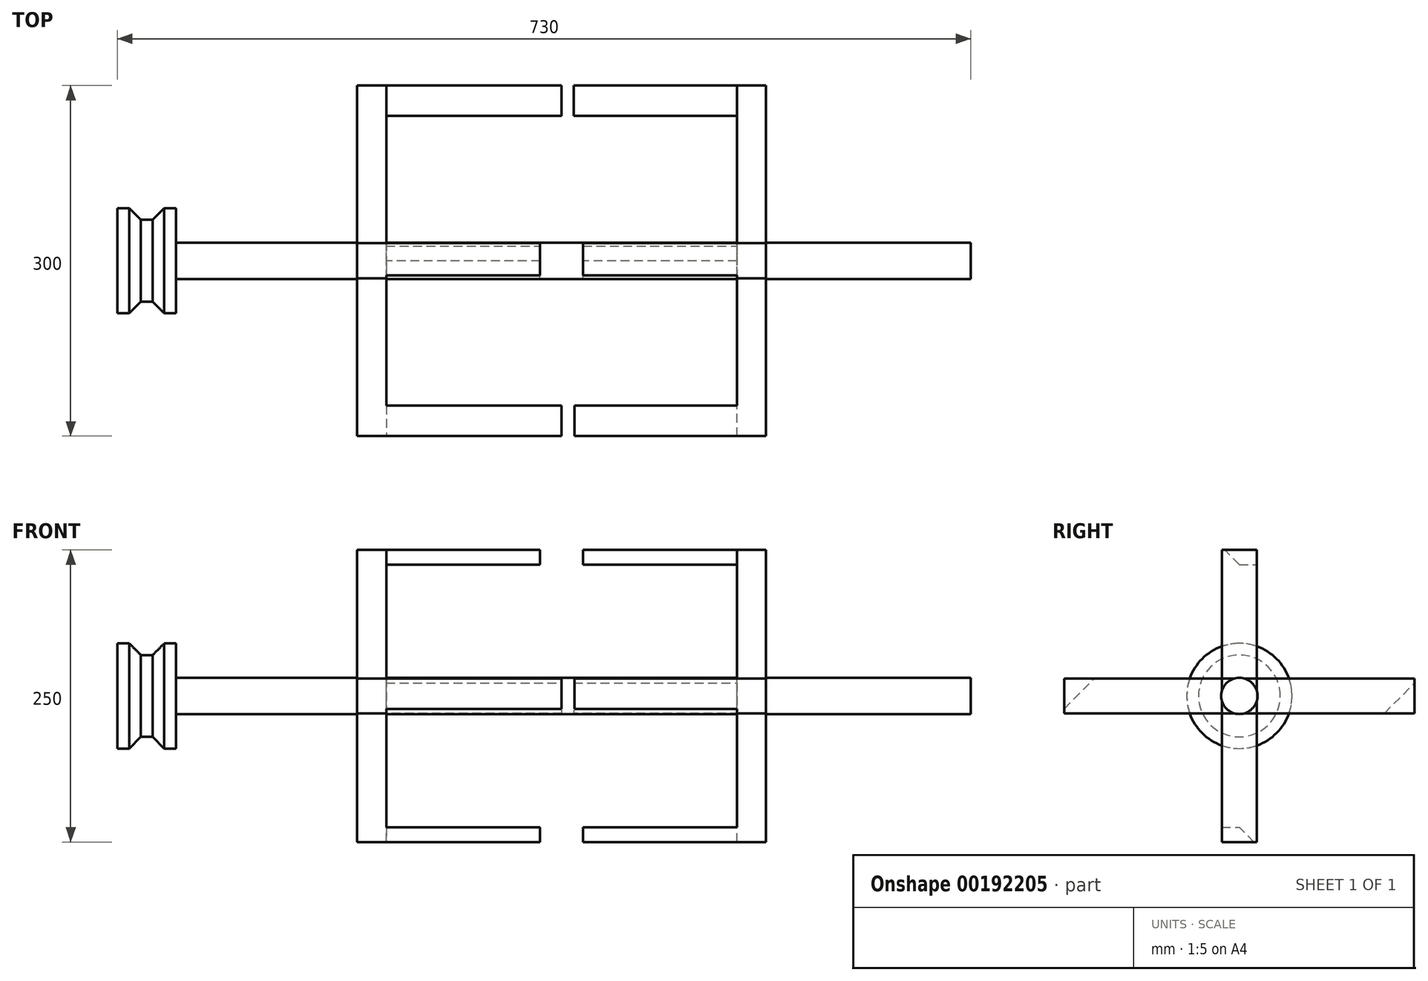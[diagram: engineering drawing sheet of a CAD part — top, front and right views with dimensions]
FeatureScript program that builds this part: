
annotation { "Feature Type Name" : "Feature", "Feature Type Description" : "" }
export const myFeature = defineFeature(function(context is Context, id is Id, definition is map)
    precondition{}
    {
        {
            var Q0;
            Q0=qCreatedBy(makeId("Front.planeOp"),FACE);
            var sketch = newSketch(context, id + "F0", { "sketchPlane" : qUnion([Q0])});
            skPoint(sketch, "E0.middle", {"position": v(0, 0) * mm});
            skLineSegment(sketch, "E1.trimOffspring", {"start": v(-83.52, 150) * mm, "end": v(-200, 150) * mm});
            skLineSegment(sketch, "E2.bottom", {"start": v(-350, 15.5) * mm, "end": v(350, 15.5) * mm});
            skLineSegment(sketch, "E2.top", {"start": v(-350, -15.5) * mm, "end": v(350, -15.5) * mm});
            skLineSegment(sketch, "E2.left", {"start": v(-350, 15.5) * mm, "end": v(-350, -15.5) * mm});
            skLineSegment(sketch, "E2.right", {"start": v(350, 15.5) * mm, "end": v(350, -15.5) * mm});
            skLineSegment(sketch, "E3", {"start": v(350, 0) * mm, "end": v(-350, 0) * mm});
            skLineSegment(sketch, "E4.bottom", {"start": v(-175, -125) * mm, "end": v(-18.4, -125) * mm});
            skLineSegment(sketch, "E4.top", {"start": v(-175, 125) * mm, "end": v(-18.4, 125) * mm});
            skLineSegment(sketch, "E4.left", {"start": v(-175, -125) * mm, "end": v(-175, 125) * mm});
            skLineSegment(sketch, "E4.right", {"start": v(175, -125) * mm, "end": v(175, 125) * mm});
            skLineSegment(sketch, "E5.bottom", {"start": v(-150, -112.5) * mm, "end": v(-18.4, -112.5) * mm});
            skLineSegment(sketch, "E5.top", {"start": v(-150, 112.5) * mm, "end": v(-18.4, 112.5) * mm});
            skLineSegment(sketch, "E5.left", {"start": v(-150, -112.5) * mm, "end": v(-150, 112.5) * mm});
            skLineSegment(sketch, "E5.right", {"start": v(150, -112.5) * mm, "end": v(150, 112.5) * mm});
            skLineSegment(sketch, "E6.left", {"start": v(-18.4, -125) * mm, "end": v(-18.4, -112.5) * mm});
            skLineSegment(sketch, "E6.right", {"start": v(18.4, -125) * mm, "end": v(18.4, -112.5) * mm});
            skPoint(sketch, "E6.middle", {"position": v(0, -112.5) * mm});
            skLineSegment(sketch, "E7.left", {"start": v(-18.4, 125) * mm, "end": v(-18.4, 112.5) * mm});
            skLineSegment(sketch, "E7.right", {"start": v(18.4, 125) * mm, "end": v(18.4, 112.5) * mm});
            skPoint(sketch, "E7.middle", {"position": v(0, 112.5) * mm});
            skPoint(sketch, "E7.cornerSnap0", {"position": v(0, 125) * mm});
            skPoint(sketch, "E8.orphan", {"position": v(18.4, 100) * mm});
            skPoint(sketch, "E9.orphan", {"position": v(-18.4, 100) * mm});
            skLineSegment(sketch, "E10.trimOffspring", {"start": v(18.4, 112.5) * mm, "end": v(150, 112.5) * mm});
            skLineSegment(sketch, "E11.trimOffspring", {"start": v(18.4, 125) * mm, "end": v(175, 125) * mm});
            skPoint(sketch, "E12.orphan", {"position": v(18.4, -100) * mm});
            skPoint(sketch, "E13.orphan", {"position": v(-18.4, -100) * mm});
            skLineSegment(sketch, "E14.trimOffspring", {"start": v(18.4, -112.5) * mm, "end": v(150, -112.5) * mm});
            skLineSegment(sketch, "E15.trimOffspring", {"start": v(18.4, -125) * mm, "end": v(175, -125) * mm});
            skSolve(sketch);
        }
        {
            var Q0;
            {var subQ0=sQuery(id+"F0.wireOp",EDGE,"E2.bottom");var subQ1=sQuery(id+"F0.wireOp",EDGE,"nP24sxVt-sFxR-fhHE-sXsC-Jo28Dy18wR9g.left");var subQ2=makeQuery(id+"F0.imprint","INTERSECT",VERTEX,{"derivedFrom":[subQ1,subQ0]});Q0=makeQuery(id+"F0.imprint","IMPRINT",FACE,{"disambiguationData":[TD([[makeQuery(id+"F0.imprint","IMPRINT",EDGE,{"disambiguationData":[TD([[subQ2,1.0]])],"derivedFrom":subQ1}),1.0]])]});}
            var Q1;
            {var subQ0=sQuery(id+"F0.wireOp",EDGE,"E2.bottom");var subQ1=sQuery(id+"F0.wireOp",EDGE,"nP24sxVt-sFxR-fhHE-sXsC-Jo28Dy18wR9g.left");var subQ2=makeQuery(id+"F0.imprint","INTERSECT",VERTEX,{"derivedFrom":[subQ1,subQ0]});Q1=makeQuery(id+"F0.imprint","IMPRINT",FACE,{"disambiguationData":[TD([[makeQuery(id+"F0.imprint","IMPRINT",EDGE,{"disambiguationData":[TD([[subQ2,1.0]])],"derivedFrom":subQ1}),-1.0]])]});}
            var Q2;
            {var subQ0=sQuery(id+"F0.wireOp",EDGE,"E2.bottom");var subQ5=sQuery(id+"F0.wireOp",EDGE,"E2.right");var subQ6=makeQuery(id+"F0.imprint","INTERSECT",VERTEX,{"derivedFrom":[subQ0,subQ5]});Q2=makeQuery(id+"F0.imprint","IMPRINT",FACE,{"disambiguationData":[TD([[makeQuery(id+"F0.imprint","IMPRINT",EDGE,{"disambiguationData":[TD([[subQ6,-1.0]])],"derivedFrom":subQ5}),-1.0]])]});}
            var Q3;
            {var subQ0=sQuery(id+"F0.wireOp",EDGE,"E2.bottom");var subQ1=sQuery(id+"F0.wireOp",EDGE,"nP24sxVt-sFxR-fhHE-sXsC-Jo28Dy18wR9g.right");var subQ2=makeQuery(id+"F0.imprint","INTERSECT",VERTEX,{"derivedFrom":[subQ1,subQ0]});Q3=makeQuery(id+"F0.imprint","IMPRINT",FACE,{"disambiguationData":[TD([[makeQuery(id+"F0.imprint","IMPRINT",EDGE,{"disambiguationData":[TD([[subQ2,1.0]])],"derivedFrom":subQ1}),1.0]])]});}
            var Q4;
            {var subQ0=sQuery(id+"F0.wireOp",EDGE,"E2.bottom");var subQ5=sQuery(id+"F0.wireOp",EDGE,"E2.left");var subQ6=makeQuery(id+"F0.imprint","INTERSECT",VERTEX,{"derivedFrom":[subQ0,subQ5]});Q4=makeQuery(id+"F0.imprint","IMPRINT",FACE,{"disambiguationData":[TD([[makeQuery(id+"F0.imprint","IMPRINT",EDGE,{"disambiguationData":[TD([[subQ6,-1.0]])],"derivedFrom":subQ5}),1.0]])]});}
            var Q5;
            Q5=sQuery(id+"F0.wireOp",EDGE,"E3");
            revolve(context, id + "F1", {"entities" : qUnion([Q0, Q1, Q2, Q3, Q4]), "axis" : qUnion([Q5]), "revolveType" : RevolveType.FULL});
        }
        {
            var Q0;
            {var subQ6=sQuery(id+"F0.wireOp",EDGE,"E4.bottom");Q0=makeQuery(id+"F0.imprint","IMPRINT",FACE,{"disambiguationData":[TD([[makeQuery(id+"F0.imprint","IMPRINT",EDGE,{"derivedFrom":subQ6}),1.0]])]});}
            var Q1;
            Q1=makeQuery(id+"F0.imprint","IMPRINT",FACE,{"disambiguationData":[TD([[makeQuery(id+"F0.imprint","IMPRINT",EDGE,{"derivedFrom":sQuery(id+"F0.wireOp",EDGE,"E6.right")}),-1.0]])]});
            var Q2;
            {var subQ1=sQuery(id+"F0.wireOp",EDGE,"E4.top");Q2=makeQuery(id+"F0.imprint","IMPRINT",FACE,{"disambiguationData":[TD([[makeQuery(id+"F0.imprint","IMPRINT",EDGE,{"derivedFrom":subQ1}),-1.0]])]});}
            var Q3;
            Q3=makeQuery(id+"F0.imprint","IMPRINT",FACE,{"disambiguationData":[TD([[makeQuery(id+"F0.imprint","IMPRINT",EDGE,{"derivedFrom":sQuery(id+"F0.wireOp",EDGE,"E7.right")}),1.0]])]});
            var Q4;
            {var subQ0=sQuery(id+"F0.wireOp",EDGE,"E4.left");var subQ1=sQuery(id+"F0.wireOp",EDGE,"E2.bottom");var subQ2=makeQuery(id+"F0.imprint","INTERSECT",VERTEX,{"derivedFrom":[subQ1,subQ0]});Q4=makeQuery(id+"F0.imprint","IMPRINT",FACE,{"disambiguationData":[TD([[makeQuery(id+"F0.imprint","IMPRINT",EDGE,{"disambiguationData":[TD([[subQ2,-1.0]])],"derivedFrom":subQ1}),-1.0]])]});}
            var Q5;
            {var subQ0=sQuery(id+"F0.wireOp",EDGE,"E4.left");var subQ1=sQuery(id+"F0.wireOp",EDGE,"E2.top");var subQ2=makeQuery(id+"F0.imprint","INTERSECT",VERTEX,{"derivedFrom":[subQ1,subQ0]});Q5=makeQuery(id+"F0.imprint","IMPRINT",FACE,{"disambiguationData":[TD([[makeQuery(id+"F0.imprint","IMPRINT",EDGE,{"disambiguationData":[TD([[subQ2,-1.0]])],"derivedFrom":subQ1}),1.0]])]});}
            var Q6;
            {var subQ0=sQuery(id+"F0.wireOp",EDGE,"E5.right");var subQ1=sQuery(id+"F0.wireOp",EDGE,"E2.bottom");var subQ2=makeQuery(id+"F0.imprint","INTERSECT",VERTEX,{"derivedFrom":[subQ1,subQ0]});Q6=makeQuery(id+"F0.imprint","IMPRINT",FACE,{"disambiguationData":[TD([[makeQuery(id+"F0.imprint","IMPRINT",EDGE,{"disambiguationData":[TD([[subQ2,-1.0]])],"derivedFrom":subQ1}),-1.0]])]});}
            var Q7;
            {var subQ0=sQuery(id+"F0.wireOp",EDGE,"E5.right");var subQ1=sQuery(id+"F0.wireOp",EDGE,"E2.top");var subQ2=makeQuery(id+"F0.imprint","INTERSECT",VERTEX,{"derivedFrom":[subQ1,subQ0]});Q7=makeQuery(id+"F0.imprint","IMPRINT",FACE,{"disambiguationData":[TD([[makeQuery(id+"F0.imprint","IMPRINT",EDGE,{"disambiguationData":[TD([[subQ2,-1.0]])],"derivedFrom":subQ1}),1.0]])]});}
            extrude(context, id + "F2", {"entities" : qUnion([Q0, Q1, Q2, Q3, Q4, Q5, Q6, Q7]), "depth" : 30 * mm, "symmetric" : true});
        }
        {
            var Q0;
            Q0=qCreatedBy(makeId("Top.planeOp"),FACE);
            var sketch = newSketch(context, id + "F3", { "sketchPlane" : qUnion([Q0])});
            skLineSegment(sketch, "E16.bottom", {"start": v(175, 150) * mm, "end": v(10.38, 150) * mm});
            skLineSegment(sketch, "E16.top", {"start": v(175, -150) * mm, "end": v(10.94, -150) * mm});
            skLineSegment(sketch, "E16.left", {"start": v(175, 150) * mm, "end": v(175, -150) * mm});
            skLineSegment(sketch, "E16.right", {"start": v(-175, 150) * mm, "end": v(-175, -150) * mm});
            skPoint(sketch, "E16.middle", {"position": v(0, 0) * mm});
            skLineSegment(sketch, "E17.bottom", {"start": v(-150, -124) * mm, "end": v(0, -124) * mm});
            skLineSegment(sketch, "E17.top", {"start": v(-150, 124) * mm, "end": v(0, 124) * mm});
            skLineSegment(sketch, "E17.left", {"start": v(-150, -124) * mm, "end": v(-150, 124) * mm});
            skLineSegment(sketch, "E17.right", {"start": v(150, -124) * mm, "end": v(150, 124) * mm});
            skLineSegment(sketch, "E18", {"start": v(10.38, 150) * mm, "end": v(10.38, 124) * mm});
            skLineSegment(sketch, "E19", {"start": v(0, 124) * mm, "end": v(0, 150) * mm});
            skLineSegment(sketch, "E20", {"start": v(10.94, -124) * mm, "end": v(10.94, -150) * mm});
            skLineSegment(sketch, "E21", {"start": v(10.94, -150) * mm, "end": v(175, -150) * mm});
            skLineSegment(sketch, "E22", {"start": v(0, -124) * mm, "end": v(0, -150) * mm});
            skLineSegment(sketch, "E23.trimOffspring", {"start": v(10.94, -124) * mm, "end": v(150, -124) * mm});
            skLineSegment(sketch, "E24.trimOffspring", {"start": v(0, -150) * mm, "end": v(-175, -150) * mm});
            skLineSegment(sketch, "E25.trimOffspring", {"start": v(0, 150) * mm, "end": v(-175, 150) * mm});
            skLineSegment(sketch, "E26.trimOffspring", {"start": v(10.38, 124) * mm, "end": v(150, 124) * mm});
            skSolve(sketch);
        }
        {
            var Q0;
            Q0 = qSketchRegion(id + "F3", true);
            extrude(context, id + "F4", {"entities" : qUnion([Q0]), "depth" : 30 * mm, "symmetric" : true});
        }
        {
            var Q0;
            Q0=makeQuery(id+"F4.opExtrude","CAP_EDGE",EDGE,{"disambiguationData":[OSD([sQuery(id+"F3.wireOp",EDGE,"E17.top")])],"isStart":false});
            var Q1;
            Q1=makeQuery(id+"F4.opExtrude","CAP_EDGE",EDGE,{"disambiguationData":[OSD([sQuery(id+"F3.wireOp",EDGE,"E26.trimOffspring")])],"isStart":false});
            var Q2;
            Q2=makeQuery(id+"F4.opExtrude","CAP_EDGE",EDGE,{"disambiguationData":[OSD([sQuery(id+"F3.wireOp",EDGE,"E17.bottom")])],"isStart":true});
            var Q3;
            Q3=makeQuery(id+"F4.opExtrude","CAP_EDGE",EDGE,{"disambiguationData":[OSD([sQuery(id+"F3.wireOp",EDGE,"E23.trimOffspring")])],"isStart":true});
            chamfer(context, id + "F5", {"entities" : qUnion([Q0, Q1, Q2, Q3]), "width" : 30 * mm, "tangentPropagation" : true});
        }
        {
            var Q0;
            Q0=makeQuery(id+"F1.opRevolve","SWEPT_FACE",FACE,{"disambiguationData":[OSD([sQuery(id+"F0.wireOp",EDGE,"E2.left")])]});
            var sketch = newSketch(context, id + "F6", { "sketchPlane" : qUnion([Q0])});
            skCircle(sketch, "E27", {"center": v(0, 0) * mm, "radius": 50 * mm});
            skSolve(sketch);
        }
        {
            var Q0;
            Q0 = qSketchRegion(id + "F6", true);
            extrude(context, id + "F7", {"entities" : qUnion([Q0]), "operationType" : NewBodyOperationType.REMOVE, "oppositeDirection" : true, "depth" : 20 * mm});
        }
        {
            var Q0;
            Q0=makeQuery(id+"F7.boolean.opBoolean","COPY",FACE,{"derivedFrom":makeQuery(id+"F7.opExtrude","CAP_FACE",FACE,{"disambiguationData":[OSD([sQuery(id+"F6.wireOp",EDGE,"E27")])],"isStart":false})});
            var sketch = newSketch(context, id + "F8", { "sketchPlane" : qUnion([Q0])});
            skCircle(sketch, "E28", {"center": v(0, 0) * mm, "radius": 45 * mm});
            skSolve(sketch);
        }
        {
            var Q0;
            Q0 = qSketchRegion(id + "F8", true);
            extrude(context, id + "F9", {"entities" : qUnion([Q0]), "operationType" : NewBodyOperationType.ADD, "depth" : 20 * mm});
        }
        {
            var Q0;
            Q0=makeQuery(id+"F9.opExtrude","CAP_FACE",FACE,{"disambiguationData":[OSD([sQuery(id+"F8.wireOp",EDGE,"E28")])],"isStart":false});
            var sketch = newSketch(context, id + "F10", { "sketchPlane" : qUnion([Q0])});
            skCircle(sketch, "E29", {"center": v(0, 0) * mm, "radius": 35 * mm});
            skSolve(sketch);
        }
        {
            var Q0;
            Q0 = qSketchRegion(id + "F10", true);
            extrude(context, id + "F11", {"entities" : qUnion([Q0]), "operationType" : NewBodyOperationType.ADD, "depth" : 10 * mm});
        }
        {
            var Q0;
            Q0=makeQuery(id+"F11.opExtrude","CAP_FACE",FACE,{"disambiguationData":[OSD([sQuery(id+"F10.wireOp",EDGE,"E29")])],"isStart":false});
            var sketch = newSketch(context, id + "F12", { "sketchPlane" : qUnion([Q0])});
            skCircle(sketch, "E30", {"center": v(0, 0) * mm, "radius": 45 * mm});
            skSolve(sketch);
        }
        {
            var Q0;
            Q0 = qSketchRegion(id + "F12", true);
            extrude(context, id + "F13", {"entities" : qUnion([Q0]), "operationType" : NewBodyOperationType.ADD, "depth" : 20 * mm});
        }
        {
            var Q0;
            Q0=makeQuery(id+"F9.opExtrude","CAP_EDGE",EDGE,{"disambiguationData":[OSD([sQuery(id+"F8.wireOp",EDGE,"E28")])],"isStart":false});
            var Q1;
            Q1=makeQuery(id+"F13.opExtrude","CAP_EDGE",EDGE,{"disambiguationData":[OSD([sQuery(id+"F12.wireOp",EDGE,"E30")])],"isStart":true});
            chamfer(context, id + "F14", {"entities" : qUnion([Q0, Q1]), "width" : 10 * mm, "tangentPropagation" : true});
        }
        {
            var Q0;
            Q0=makeQuery(id+"F2.opExtrude","CAP_EDGE",EDGE,{"disambiguationData":[OSD([sQuery(id+"F0.wireOp",EDGE,"E5.top")])],"isStart":false});
            var Q1;
            Q1=makeQuery(id+"F2.opExtrude","CAP_EDGE",EDGE,{"disambiguationData":[OSD([sQuery(id+"F0.wireOp",EDGE,"E10.trimOffspring")])],"isStart":false});
            chamfer(context, id + "F15", {"entities" : qUnion([Q0, Q1]), "width" : 15 * mm, "tangentPropagation" : true});
        }
        {
            var Q0;
            Q0=makeQuery(id+"F2.opExtrude","CAP_EDGE",EDGE,{"disambiguationData":[OSD([sQuery(id+"F0.wireOp",EDGE,"E5.bottom")])],"isStart":true});
            var Q1;
            Q1=makeQuery(id+"F2.opExtrude","CAP_EDGE",EDGE,{"disambiguationData":[OSD([sQuery(id+"F0.wireOp",EDGE,"E14.trimOffspring")])],"isStart":true});
            chamfer(context, id + "F16", {"entities" : qUnion([Q0, Q1]), "width" : 15 * mm, "tangentPropagation" : true});
        }
        {
            var Q0;
            {var subQ0=sQuery(id+"F0.wireOp",EDGE,"E5.left");var subQ1=sQuery(id+"F0.wireOp",EDGE,"E2.top");var subQ2=makeQuery(id+"F0.imprint","INTERSECT",VERTEX,{"derivedFrom":[subQ1,subQ0]});Q0=makeQuery(id+"F0.imprint","IMPRINT",FACE,{"disambiguationData":[TD([[makeQuery(id+"F0.imprint","IMPRINT",EDGE,{"disambiguationData":[TD([[subQ2,-1.0]])],"derivedFrom":subQ1}),1.0]])]});}
            var Q1;
            Q1=sQuery(id+"F0.wireOp",EDGE,"E3");
            revolve(context, id + "F17", {"entities" : qUnion([Q0]), "axis" : qUnion([Q1]), "revolveType" : RevolveType.FULL});
        }
    });
